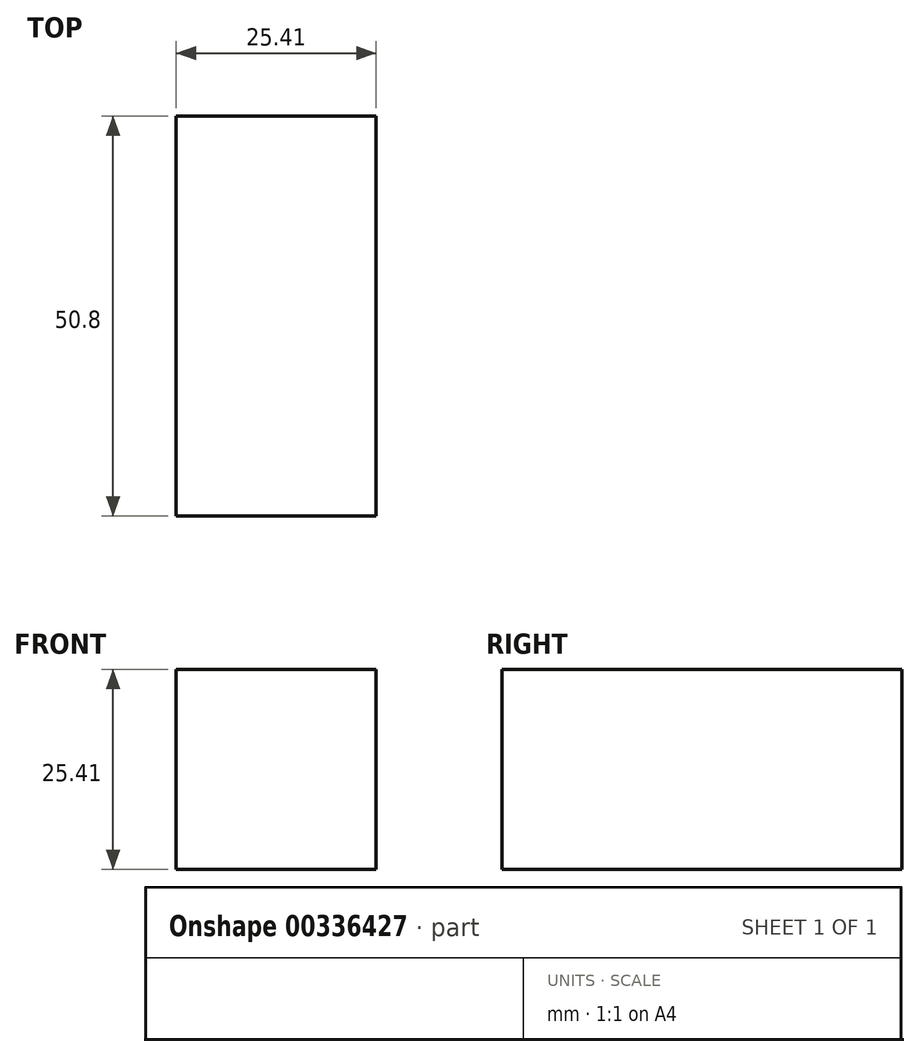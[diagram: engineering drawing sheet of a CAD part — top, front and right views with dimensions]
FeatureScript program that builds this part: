
annotation { "Feature Type Name" : "Feature", "Feature Type Description" : "" }
export const myFeature = defineFeature(function(context is Context, id is Id, definition is map)
    precondition{}
    {
        {
            var Q0;
            Q0=qCreatedBy(makeId("Front.planeOp"),FACE);
            var sketch = newSketch(context, id + "F0", { "sketchPlane" : qUnion([Q0])});
            skLineSegment(sketch, "E0.bottom", {"start": v(0, 0) * mm, "end": v(25.4, 0) * mm});
            skLineSegment(sketch, "E0.top", {"start": v(0, 25.4) * mm, "end": v(25.4, 25.4) * mm});
            skLineSegment(sketch, "E0.left", {"start": v(0, 0) * mm, "end": v(0, 25.4) * mm});
            skLineSegment(sketch, "E0.right", {"start": v(25.4, 0) * mm, "end": v(25.4, 25.4) * mm});
            skSolve(sketch);
        }
        {
            var Q0;
            Q0 = qSketchRegion(id + "F0", true);
            extrude(context, id + "F1", {"entities" : qUnion([Q0]), "endBound" : BoundingType.SYMMETRIC, "depth" : 50.8 * mm});
        }
    });
